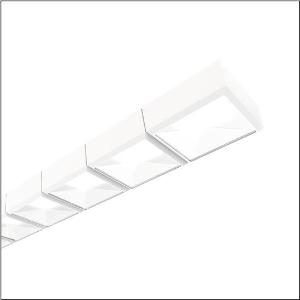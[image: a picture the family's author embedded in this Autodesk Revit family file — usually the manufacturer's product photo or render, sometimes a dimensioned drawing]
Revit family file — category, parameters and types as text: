
# Revit family: scriptus_r__11_5mz214d0twa_b782
name_source: partatom
category: Lighting Fixtures
units: mm (PartAtom-declared; Revit-internal decimal feet)

## family parameters
Cut with Voids When Loaded = No
Host = Face
Light Source = No
Part Type = Normal
Room Calculation Point = No
Round Connector Dimension = Use Diameter
Shared = No

## types (1)
- --- (1 x LED 3000K+6500K / CRI = 80 (unbekannt), 3600 lm, 3000K)
    Apparent Load = 53 VA
    CIE Flux Codes = 82 95 99 100 100
    Color Rendering = 80
    Color Temperature = 3000K
    Default Elevation = 1800 mm
    Description = Scriptus® 11, office luminaire, primary optical cover: lenses, CAT 2 (L<= 3000cd/m²), light emission: direct distribution, primary light characteristic: symmetric, installation type: surface-mounted, LED, rated luminous flux: 7.190lm, luminous efficacy: 137lm/W, light colour: 8tw, colour temperature: 3000..6500K, control gear: ECG DALI, with terminal, 5-pole, mains connection: 230V, AC, 50Hz, rated input power: 53W, housing, luminaire housing, of aluminium, traffic white (RAL 9016), length: 3.088mm, width: 114mm, height: 57mm, protection rating (complete): IP20, insulation class (complete): insulation class I (protective earthing), certification: CE, protection symbol: F, permissible operating ambient temperature: 0..+35°C, standard: EN 50419, packaging unit: 1 piece
    Height = 57 mm
    Lamp = 1 x LED 3000K+6500K / CRI >= 80 (unbekannt)
    Lamp Light Flux = 3600 lm
    Lamp count = 1
    Length = 3088 mm
    Luminous efficacy = 137 lm/W
    Manufacturer = Siteco
    ModVariant = No
    Model = 5MZ214D0TWA
    Mounting Place = Ceiling
    Mounting Type = Surface mounted
    Number of Poles = 1
    OnlyDefault = Yes
    Power Factor = 1
    Product Name = Scriptus® 11
    Product group = office luminaire | ceiling mounted
    ProductGroupID = 304
    Protection Class = Protection class I
    Protection Degree = IP 20
    RLX_Detail_Level = 1
    RLX_Emergency_Light_Flux = 0 lm
    RLX_Emergency_Type = 0
    RLX_Emergency_Type_DB = No
    RlxData = <blob elided: 30477 chars, md5=9d94adb6>
    Socket = socket
    Standby Power = 0 W
    System Light Flux = 7200 lm
    System Power = 53 W
    Type Comments = individual setting: colour temperature 6500K
    Type Image = l_1004833.jpg
    URL = http://relux.com
    VarID = @adj_149057
    Voltage = 0 V
    Weight = 0.00 kg
    Width = 114 mm

## geometry (parser evidence)
native form markers: Blend x4, Sweep x13
no freeform markers — native parametric forms only
